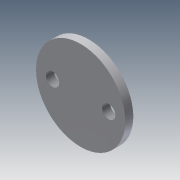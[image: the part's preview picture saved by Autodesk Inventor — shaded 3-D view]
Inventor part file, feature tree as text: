
AUTODESK INVENTOR PART (.ipt)
format: ipt  version: 2013 (Build 170138000, 138)  size: 103,424 bytes
history: native  units: mm
features: sketch x5, extrude x4
ambient origin geometry x8: Origin, YZ Plane, XZ Plane, XY Plane, X Axis, Y Axis, Z Axis, Center Point
bodies: Solid1 (feature_tree)
feature tree (9):
  sketch  "Sketch1"  dims[d0=20.0mm d1=1.8mm d2=0.0mm]
  sketch  "Sketch2"  dims[d3=7.0mm d4=5.0mm]
  extrude  "Extrusion1"  Depth=1.8mm TaperAngle=0.0deg
  extrude  "Extrusion2"  Depth=5.0mm
  extrude  "Extrusion3"  Depth=6.3mm
  extrude  "Extrusion4"  Depth=2.4mm TaperAngle=0.0deg
  sketch  "Sketch3"  dims[d5=2.4mm d6=0.0mm d7=6.3mm]
  sketch  "Sketch4"  dims[d8=3.0mm d9=2.4mm d10=0.0mm]
  sketch  "Sketch5"  dims[d11=6.3mm d12=3.0mm d13=2.0mm d14=0.0mm]
